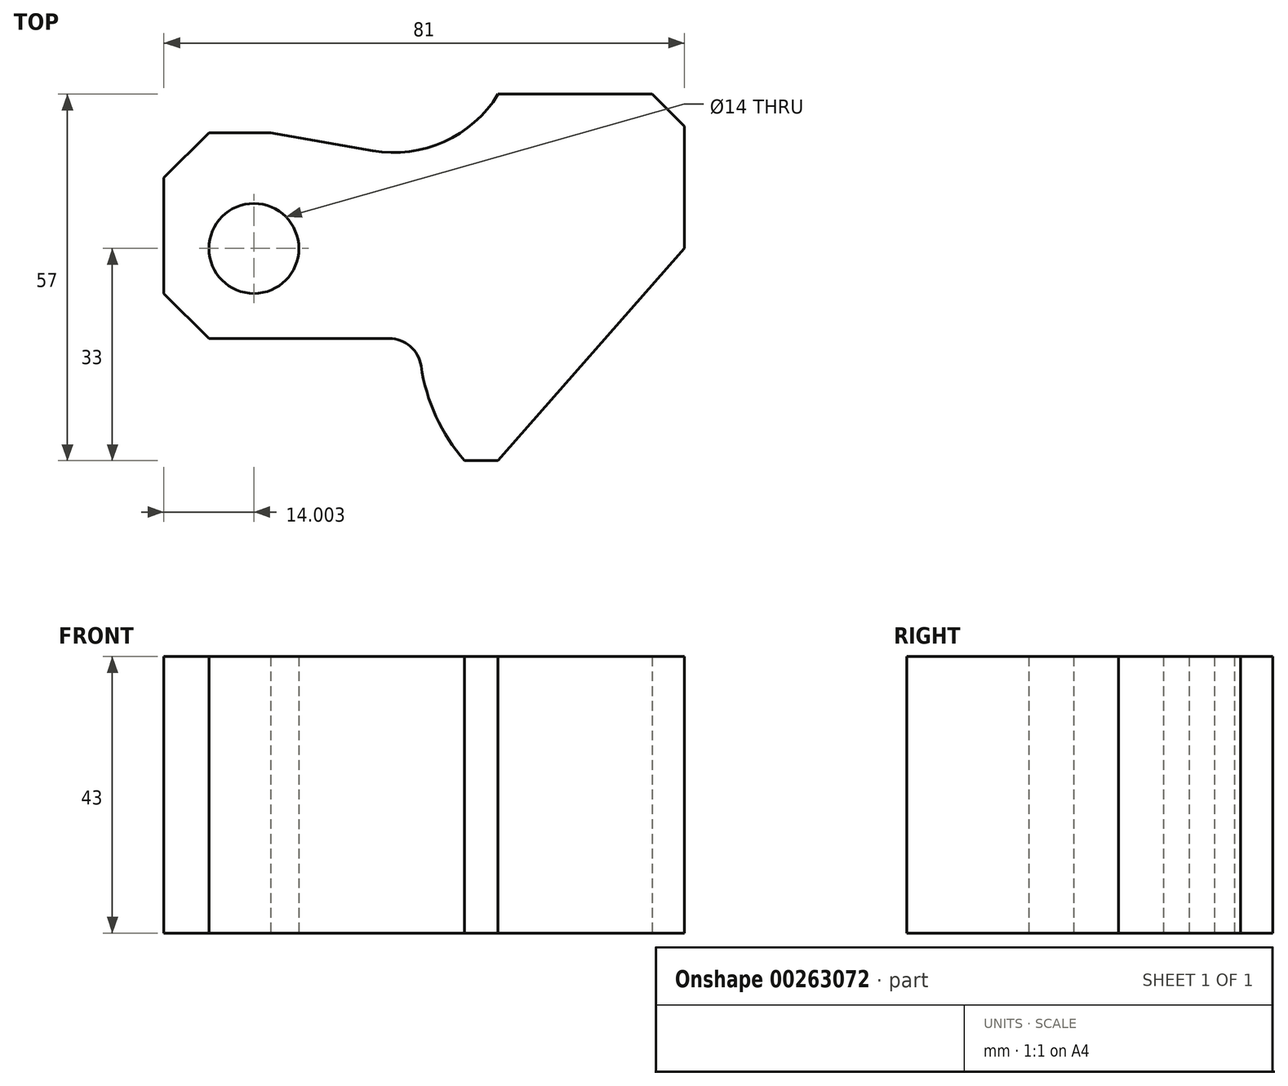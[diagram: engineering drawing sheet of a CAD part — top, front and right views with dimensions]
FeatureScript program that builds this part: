
annotation { "Feature Type Name" : "Feature", "Feature Type Description" : "" }
export const myFeature = defineFeature(function(context is Context, id is Id, definition is map)
    precondition{}
    {
        {
            var Q0;
            Q0=qCreatedBy(makeId("Top.planeOp"),FACE);
            var sketch = newSketch(context, id + "F0", { "sketchPlane" : qUnion([Q0])});
            skLineSegment(sketch, "E0", {"start": v(-29.76, 7) * mm, "end": v(-36.76, 0) * mm});
            skLineSegment(sketch, "E1", {"start": v(-36.76, 0) * mm, "end": v(-36.76, -18) * mm});
            skLineSegment(sketch, "E2", {"start": v(-36.76, -18) * mm, "end": v(-29.76, -25) * mm});
            skLineSegment(sketch, "E3", {"start": v(15.24, 13) * mm, "end": v(39.24, 13) * mm});
            skLineSegment(sketch, "E4", {"start": v(39.24, 13) * mm, "end": v(44.24, 8) * mm});
            skLineSegment(sketch, "E5", {"start": v(44.24, 8) * mm, "end": v(44.24, -11) * mm});
            skLineSegment(sketch, "E6", {"start": v(-29.76, -25) * mm, "end": v(-1.7, -25) * mm});
            skPoint(sketch, "E7.visualSharp", {"position": v(21.16, -25) * mm});
            skLineSegment(sketch, "E8", {"start": v(15.24, -44) * mm, "end": v(10.03, -44) * mm});
            skLineSegment(sketch, "E9", {"start": v(15.24, -44) * mm, "end": v(44.24, -11) * mm});
            skCircle(sketch, "E10", {"center": v(-22.76, -11) * mm, "radius": 7 * mm});
            skLineSegment(sketch, "E11", {"start": v(-36.76, 0) * mm, "end": v(-36.76, 34.55) * mm, "construction": true});
            skLineSegment(sketch, "E12", {"start": v(-36.76, -18) * mm, "end": v(-36.76, -32.81) * mm, "construction": true});
            skLineSegment(sketch, "E13", {"start": v(44.24, 8) * mm, "end": v(44.24, 28.08) * mm, "construction": true});
            skLineSegment(sketch, "E14", {"start": v(-29.76, 7) * mm, "end": v(-20.12, 7) * mm});
            skLineSegment(sketch, "E15", {"start": v(-20.12, 7) * mm, "end": v(-4.26, 4.2) * mm});
            skPoint(sketch, "E16.visualSharp", {"position": v(5.22, -25) * mm});
            skArc(sketch, "E16.filletArc", {"start": v(3.26, -29.26) * mm, "mid": v(1.57, -26.21) * mm, "end": v(-1.7, -25) * mm});
            skPoint(sketch, "E17", {"position": v(31.94, -25) * mm});
            skArc(sketch, "E18", {"start": v(3.26, -29.26) * mm, "mid": v(5.6, -37.12) * mm, "end": v(10.03, -44) * mm});
            skLineSegment(sketch, "E19", {"start": v(-20.12, 7) * mm, "end": v(-4.15, 7) * mm, "construction": true});
            skArc(sketch, "E20", {"start": v(-4.26, 4.2) * mm, "mid": v(6.85, 5.6) * mm, "end": v(15.24, 13) * mm});
            skSolve(sketch);
        }
        {
            var Q0;
            Q0 = qSketchRegion(id + "F0", true);
            extrude(context, id + "F1", {"entities" : qUnion([Q0]), "depth" : 43 * mm});
        }
    });
